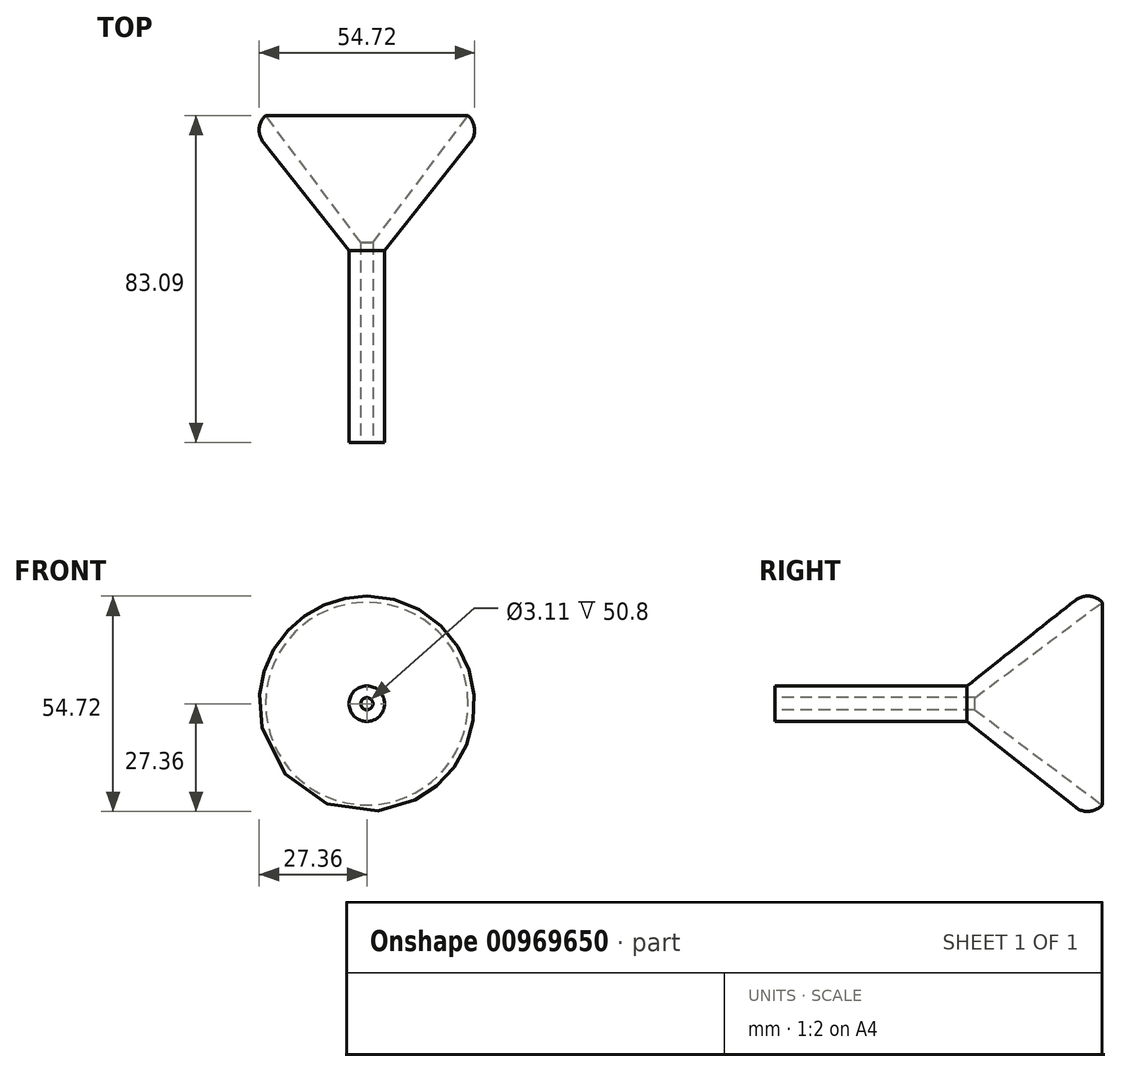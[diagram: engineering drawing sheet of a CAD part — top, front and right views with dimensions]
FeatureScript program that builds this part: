
annotation { "Feature Type Name" : "Feature", "Feature Type Description" : "" }
export const myFeature = defineFeature(function(context is Context, id is Id, definition is map)
    precondition{}
    {
        {
            var Q0;
            Q0=qCreatedBy(makeId("Top.planeOp"),FACE);
            var sketch = newSketch(context, id + "F0", { "sketchPlane" : qUnion([Q0])});
            skLineSegment(sketch, "E0", {"start": v(0, 0) * mm, "end": v(0, -48.76) * mm});
            skLineSegment(sketch, "E1", {"start": v(0, -48.76) * mm, "end": v(4.52, -48.76) * mm});
            skLineSegment(sketch, "E2", {"start": v(4.52, -48.76) * mm, "end": v(4.52, 0) * mm});
            skLineSegment(sketch, "E3", {"start": v(4.52, 0) * mm, "end": v(29.4, 31.43) * mm});
            skLineSegment(sketch, "E4", {"start": v(29.4, 31.43) * mm, "end": v(25.75, 34.33) * mm});
            skLineSegment(sketch, "E5", {"start": v(25.75, 34.33) * mm, "end": v(0, 0) * mm});
            skSolve(sketch);
        }
        {
            var Q0;
            Q0 = qSketchRegion(id + "F0", true);
            var Q1;
            Q1=sQuery(id+"F0.wireOp",EDGE,"E0");
            revolve(context, id + "F1", {"surfaceOperationType" : NewSurfaceOperationType.NEW, "entities" : qUnion([Q0]), "axis" : qUnion([Q1]), "revolveType" : RevolveType.FULL});
        }
        {
            var Q0;
            Q0=makeQuery(id+"F1.opRevolve","SWEPT_FACE",FACE,{"disambiguationData":[OSD([sQuery(id+"F0.wireOp",EDGE,"E1")])]});
            var sketch = newSketch(context, id + "F2", { "sketchPlane" : qUnion([Q0])});
            skCircle(sketch, "E6", {"center": v(0, 0) * mm, "radius": 1.55 * mm});
            skSolve(sketch);
        }
        {
            var Q0;
            Q0 = qSketchRegion(id + "F2", true);
            extrude(context, id + "F3", {"entities" : qUnion([Q0]), "operationType" : NewBodyOperationType.REMOVE, "oppositeDirection" : true, "depth" : 50.8 * mm, "offsetDistance" : 25.4 * mm});
        }
        {
            var Q0;
            Q0=makeQuery(id+"F1.opRevolve","SWEPT_EDGE",EDGE,{"disambiguationData":[OSD([sQuery(id+"F0.wireOp",EDGE,"E3"),sQuery(id+"F0.wireOp",EDGE,"E4")])]});
            fillet(context, id + "F4", {"entities" : qUnion([Q0]), "radius" : 5.08 * mm, "tangentPropagation" : true, "allowEdgeOverflow" : false});
        }
    });
